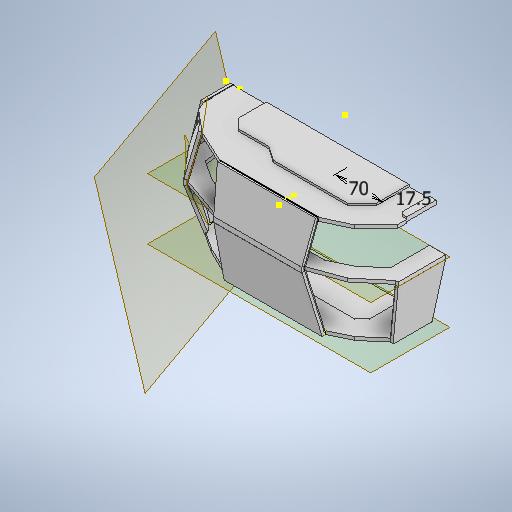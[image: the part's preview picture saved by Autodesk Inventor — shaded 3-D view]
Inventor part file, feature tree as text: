
AUTODESK INVENTOR PART (.ipt)
format: ipt  version: 2025.2 (Build 292293000, 293)  size: 5,293,056 bytes
history: native  units: mm
features: sketch x28, extrude x20, other x15, loft x7, plane x5
ambient origin geometry x8: Origin, YZ Plane, XZ Plane, XY Plane, X Axis, Y Axis, Z Axis, Center Point
bodies: Body1 (feature_tree)
feature tree (75):
  extrude  "Extrusion2"  Depth=45.0mm
  extrude  "Extrusion3"  Depth=40.0mm
  plane  "Work Plane3"
  extrude  "Extrusion4"  Depth=145.0mm
  extrude  "Extrusion5"  Depth=55.0mm
  plane  "Work Plane4"
  extrude  "Extrusion6"  Depth=40.0mm
  sketch  "Sketch8"  dims[d17=165.0deg d18=15.0mm]
  sketch  "Sketch9"  dims[d20=10.0mm d21=40.0mm]
  sketch  "Sketch10"  dims[d22=5.0mm d23=5.0mm]
  loft  "Loft1"
  loft  "Loft2"
  extrude  "Extrusion7"  Depth=5.0mm
  extrude  "Extrusion8"  TaperAngle=90.0deg  [1 undecoded]
  extrude  "Extrusion9"  Depth=30.0mm
  sketch  "Sketch14"  dims[d30=45.0mm d31=20.0mm]
  sketch  "Sketch15"  dims[d32=45.0deg d39=5.0mm d40=0.0mm]
  sketch  "Sketch16"  dims[d41=3.0mm d42=3.0mm d43=0.0mm d44=0.0mm d45=150.0mm]
  loft  "Loft3"
  loft  "Loft4"
  loft  "Loft5"
  extrude  "Extrusion10"  Depth=3.0mm
  extrude  "Extrusion11"  Depth=10.0mm
  extrude  "Extrusion12"  Depth=10.0mm
  extrude  "Extrusion13"  Depth=10.0mm
  extrude  "Extrusion14"  Depth=10.0mm
  loft  "Loft7"
  loft  "Loft8"
  sketch  "Sketch22"  dims[d57=10.0mm d58=10.0mm]
  plane  "Work Plane5"
  extrude  "Extrusion15"  Depth=3.0mm TaperAngle=0.0deg
  plane  "Work Plane6"
  extrude  "Extrusion16"  Depth=10.0mm
  extrude  "Extrusion17"  Depth=50.0mm
  plane  "Work Plane7"
  extrude  "Extrusion18"  Depth=50.0mm
  sketch  "Sketch28"  dims[d71=27.925268mm d72=10.0mm]
  extrude  "Extrusion19"  Depth=10.0mm
  extrude  "Extrusion20"  Depth=50.0mm
  extrude  "Extrusion21"  Depth=5.0mm TaperAngle=0.0deg
  sketch  "Sketch1"  dims[d6=115.0mm d8=45.0mm]
  other  "Image1"
  sketch  "Sketch3"  dims[d9=45.0deg d10=40.0mm]
  sketch  "Sketch4"  dims[d11=27.925268mm d12=145.0mm]
  sketch  "Sketch5"  dims[d13=27.052603mm d14=55.0mm]
  sketch  "Sketch6"  dims[d15=27.052603mm d16=40.0mm]
  other  "Edges1"
  other  "Edges2"
  other  "Edges3"
  other  "Edges4"
  sketch  "Sketch11"  dims[d24=40.0mm d25=90.0deg]
  sketch  "Sketch12"  dims[d26=30.0mm d27=110.0mm]
  sketch  "Sketch13"  dims[d28=25.0mm d29=25.307274mm]
  other  "Edges5"
  other  "Edges6"
  other  "Edges7"
  other  "Edges8"
  other  "Edges9"
  other  "Edges10"
  sketch  "Sketch17"  dims[d46=10.0mm d48=10.0mm]
  sketch  "Sketch18"  dims[d49=10.0mm d50=22.68928mm]
  sketch  "Sketch19"  dims[d51=10.0mm d52=10.0mm]
  sketch  "Sketch20"  dims[d53=10.0mm d54=10.0mm]
  sketch  "Sketch21"  dims[d55=10.0mm d56=10.0mm]
  other  "Edges13"
  other  "Edges14"
  other  "Edges15"
  other  "Edges16"
  sketch  "Sketch23"  dims[d59=5.0mm d60=0.0mm d61=3.0mm d62=3.0mm d63=0.0mm d64=0.0mm]
  sketch  "Sketch24"  dims[d65=-90.0mm d66=10.0mm]
  sketch  "Sketch25"  dims[d67=70.0mm d68=50.0mm]
  sketch  "Sketch26"  dims[d69=22.68928mm d70=50.0mm]
  sketch  "Sketch29"  dims[d73=50.0mm d74=60.0mm]
  sketch  "Sketch30"  dims[d75=70.0mm d76=5.0mm d77=0.0mm]
  sketch  "Sketch31"  dims[d78=0.0mm d79=90.0deg d80=0.0mm d81=90.0deg d82=0.0mm d83=90.0deg d84=0.0mm d85=90.0deg d86=4.0mm d87=0.0mm d88=4.0mm d89=0.0mm d90=4.0mm d91=0.0mm d92=0.0mm d93=90.0deg d94=0.0mm d95=90.0deg d96=0.0mm d97=90.0deg d98=0.0mm d99=90.0deg d100=0.0mm d101=90.0deg d102=0.0mm d103=90.0deg d104=4.0mm d105=0.0mm d106=4.0mm d107=0.0mm d108=4.0mm d109=0.0mm d110=4.0mm d111=0.0mm d112=4.0mm d113=0.0mm d118=0.0mm d119=90.0deg d120=0.0mm d121=90.0deg d122=0.0mm d123=90.0deg d124=0.0mm d125=90.0deg d126=4.0mm d127=0.0mm d128=4.0mm d129=0.0mm d130=4.0mm d131=0.0mm d132=92.689mm d133=4.0mm d134=0.0mm d135=70.0mm d136=17.5mm d137=5.0mm d138=25.0mm d139=70.0mm d140=25.0mm d141=17.5mm d142=90.0deg d143=23.0mm d144=0.0mm d145=70.0mm d146=3.0mm d147=17.5mm d148=0.0mm d149=25.0mm d150=30.0mm d151=15.0deg d152=90.0deg d153=5.0mm d154=20.0mm d155=90.0deg d156=4.363323mm d157=17.5mm d158=0.0mm]
note: 1 required parameter value undecoded (feature->parameter linkage not recoverable at this tier; creation-order binding heuristic only, values carry confidence <= 0.55)
